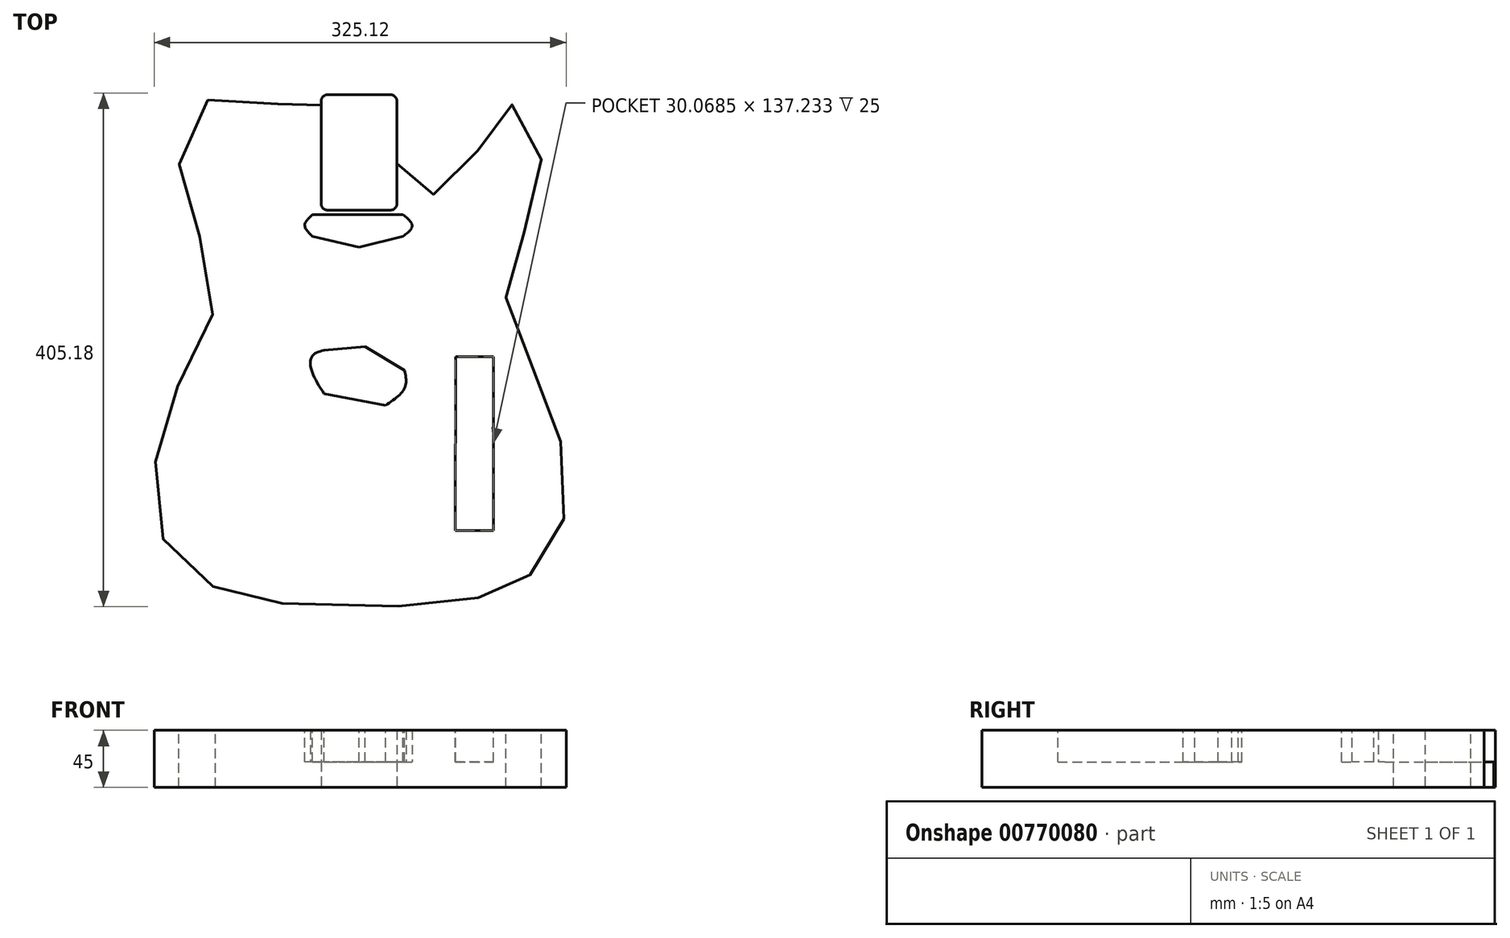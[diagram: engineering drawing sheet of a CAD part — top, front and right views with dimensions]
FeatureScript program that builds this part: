
annotation { "Feature Type Name" : "Feature", "Feature Type Description" : "" }
export const myFeature = defineFeature(function(context is Context, id is Id, definition is map)
    precondition{}
    {
        {
            var Q0;
            Q0=qCreatedBy(makeId("Top.planeOp"),FACE);
            var sketch = newSketch(context, id + "F0", { "sketchPlane" : qUnion([Q0])});
            skLineSegment(sketch, "E0.bottom", {"start": v(170, 207.5) * mm, "end": v(-170, 207.5) * mm});
            skLineSegment(sketch, "E0.top", {"start": v(170, -207.5) * mm, "end": v(-170, -207.5) * mm});
            skLineSegment(sketch, "E0.left", {"start": v(170, 207.5) * mm, "end": v(170, -207.5) * mm});
            skLineSegment(sketch, "E0.right", {"start": v(-170, 207.5) * mm, "end": v(-170, -207.5) * mm});
            skPoint(sketch, "E0.middle", {"position": v(0, 0) * mm});
            skLineSegment(sketch, "E1", {"start": v(-29.87, 193.13) * mm, "end": v(-29.87, 115.48) * mm});
            skLineSegment(sketch, "E2", {"start": v(-24.87, 110.48) * mm, "end": v(24.87, 110.48) * mm});
            skLineSegment(sketch, "E3", {"start": v(29.87, 115.48) * mm, "end": v(29.87, 147.1) * mm});
            skFitSpline(sketch, "E4", {"points": [v(29.87, 147.1) * mm, v(32.83, 137.03) * mm, v(40.54, 127.4) * mm, v(48.46, 123.11) * mm, v(60.88, 123.11) * mm, v(72.66, 126.75) * mm, v(84.65, 138.96) * mm, v(94.07, 158.01) * mm, v(99.85, 174.71) * mm, v(106.7, 187.78) * mm, v(117.41, 193.56) * mm, v(126.83, 191.42) * mm, v(137.54, 179.21) * mm, v(143.1, 164.44) * mm, v(143.1, 135.96) * mm, v(139.68, 119.26) * mm, v(132.4, 97.63) * mm, v(124.26, 79) * mm, v(119.13, 64.01) * mm, v(116.13, 46.45) * mm, v(118.27, 27.6) * mm, v(127.05, 6.2) * mm, v(137.75, -15.43) * mm, v(147.4, -36.63) * mm, v(154.88, -58.25) * mm, v(161.52, -82.88) * mm, v(163.45, -106.43) * mm, v(162.6, -128.49) * mm, v(156.81, -149.26) * mm, v(148.46, -163.18) * mm, v(137.54, -175.17) * mm, v(129.4, -181.6) * mm, v(117.63, -188.02) * mm, v(105.85, -192.3) * mm, v(92.15, -195.72) * mm, v(74.59, -198.94) * mm, v(55.53, -200.86) * mm, v(0, -202.36) * mm, v(-51.53, -200.22) * mm, v(-76.37, -198.5) * mm, v(-95, -194.87) * mm, v(-112.56, -187.8) * mm, v(-127.55, -179.66) * mm, v(-143.82, -166.17) * mm, v(-153.89, -150.11) * mm, v(-160.1, -134.7) * mm, v(-161.38, -101.08) * mm, v(-160.1, -84.38) * mm, v(-154.53, -60.4) * mm, v(-146.18, -35.99) * mm, v(-136.97, -15.86) * mm, v(-123.9, 8.55) * mm, v(-115.13, 29.97) * mm, v(-114.27, 59.3) * mm, v(-121.12, 79.43) * mm, v(-130.76, 101.06) * mm, v(-138.04, 124.82) * mm, v(-141.25, 141.74) * mm, v(-141.25, 166.15) * mm, v(-133.76, 184.56) * mm, v(-118.77, 197.63) * mm, v(-99.5, 202.76) * mm, v(-77.87, 199.55) * mm, v(-60.95, 192.7) * mm, v(-45.75, 185) * mm, v(-40.83, 183.5) * mm, v(-34.19, 186.7) * mm, v(-29.87, 193.13) * mm], "startDerivative": vector(179, -913.5) * mm, "endDerivative": vector(365.97, 729.24) * mm});
            skLineSegment(sketch, "E5", {"start": v(-29.87, 193.13) * mm, "end": v(-29.87, 196.51) * mm});
            skLineSegment(sketch, "E6", {"start": v(29.87, 147.1) * mm, "end": v(29.87, 196.51) * mm});
            skLineSegment(sketch, "E7", {"start": v(-24.87, 201.51) * mm, "end": v(24.87, 201.51) * mm});
            skPoint(sketch, "E8.visualSharp", {"position": v(-29.87, 201.51) * mm});
            skArc(sketch, "E8.filletArc", {"start": v(-24.87, 201.51) * mm, "mid": v(-28.4, 200.05) * mm, "end": v(-29.87, 196.51) * mm});
            skPoint(sketch, "E9.visualSharp", {"position": v(29.87, 201.51) * mm});
            skArc(sketch, "E9.filletArc", {"start": v(29.87, 196.51) * mm, "mid": v(28.4, 200.05) * mm, "end": v(24.87, 201.51) * mm});
            skPoint(sketch, "E10.visualSharp", {"position": v(-29.87, 110.48) * mm});
            skArc(sketch, "E10.filletArc", {"start": v(-29.87, 115.48) * mm, "mid": v(-28.4, 111.94) * mm, "end": v(-24.87, 110.48) * mm});
            skPoint(sketch, "E11.visualSharp", {"position": v(29.87, 110.48) * mm});
            skArc(sketch, "E11.filletArc", {"start": v(24.87, 110.48) * mm, "mid": v(28.4, 111.94) * mm, "end": v(29.87, 115.48) * mm});
            skLineSegment(sketch, "E12", {"start": v(0, 0) * mm, "end": v(0, 0) * mm});
            skLineSegment(sketch, "E13", {"start": v(49.42, 0) * mm, "end": v(50, 0) * mm, "construction": true});
            skPoint(sketch, "E14.trimOffspring.end.orphan", {"position": v(0, 201.51) * mm});
            skPoint(sketch, "E15.start.orphan", {"position": v(0, -202.26) * mm});
            skLineSegment(sketch, "E16", {"start": v(163.22, -99.32) * mm, "end": v(181.56, -99.32) * mm, "construction": true});
            skLineSegment(sketch, "E17", {"start": v(-161.35, -100.15) * mm, "end": v(-180.86, -100.15) * mm, "construction": true});
            skPoint(sketch, "E18.orphan", {"position": v(48.46, -201.22) * mm});
            skPoint(sketch, "E19.orphan", {"position": v(-50, -200.3) * mm});
            skPoint(sketch, "E20.orphan", {"position": v(-50, -100.15) * mm});
            skPoint(sketch, "E21.start.orphan", {"position": v(-50, 0) * mm});
            skSolve(sketch);
        }
        {
            var Q0;
            Q0=makeQuery(id+"F0.imprint","IMPRINT",FACE,{"disambiguationData":[TD([[makeQuery(id+"F0.imprint","IMPRINT",EDGE,{"derivedFrom":sQuery(id+"F0.wireOp",EDGE,"E1")}),1.0]])]});
            extrude(context, id + "F1", {"entities" : qUnion([Q0]), "depth" : 20 * mm, "offsetDistance" : 25 * mm});
        }
        {
            var Q0;
            Q0=makeQuery(id+"F0.imprint","IMPRINT",FACE,{"disambiguationData":[TD([[makeQuery(id+"F0.imprint","IMPRINT",EDGE,{"derivedFrom":sQuery(id+"F0.wireOp",EDGE,"E1")}),-1.0]])]});
            extrude(context, id + "F2", {"entities" : qUnion([Q0]), "operationType" : NewBodyOperationType.ADD, "depth" : 45 * mm, "offsetDistance" : 25 * mm});
        }
        {
            var Q0;
            Q0=makeQuery(id+"F2.opExtrude","CAP_FACE",FACE,{"disambiguationData":[OSD([sQuery(id+"F0.wireOp",EDGE,"E1"),sQuery(id+"F0.wireOp",EDGE,"E2"),sQuery(id+"F0.wireOp",EDGE,"E3"),sQuery(id+"F0.wireOp",EDGE,"E4"),sQuery(id+"F0.wireOp",EDGE,"E10.filletArc"),sQuery(id+"F0.wireOp",EDGE,"E11.filletArc")])],"isStart":false});
            var sketch = newSketch(context, id + "F3", { "sketchPlane" : qUnion([Q0])});
            skLineSegment(sketch, "E22", {"start": v(-36.68, 106.89) * mm, "end": v(34.75, 106.89) * mm});
            skFitSpline(sketch, "E23", {"points": [v(34.75, 106.89) * mm, v(42, 98.18) * mm, v(34.75, 89.76) * mm], "startDerivative": vector(21.74, -17.44) * mm, "endDerivative": vector(-21.81, -16.82) * mm});
            skLineSegment(sketch, "E24", {"start": v(34.75, 89.76) * mm, "end": v(0, 81.34) * mm});
            skLineSegment(sketch, "E25", {"start": v(0, 81.34) * mm, "end": v(-36.68, 89.76) * mm});
            skFitSpline(sketch, "E26", {"points": [v(-36.68, 106.89) * mm, v(-42.78, 98.47) * mm, v(-36.68, 89.76) * mm], "startDerivative": vector(-18.33, -16.84) * mm, "endDerivative": vector(18.26, -17.42) * mm});
            skLineSegment(sketch, "E27", {"start": v(76.35, -5.23) * mm, "end": v(106.18, -5.23) * mm});
            skLineSegment(sketch, "E28", {"start": v(106.18, -5.23) * mm, "end": v(106.18, -141.47) * mm});
            skLineSegment(sketch, "E29", {"start": v(106.18, -141.47) * mm, "end": v(106.18, -142.46) * mm});
            skLineSegment(sketch, "E30", {"start": v(106.18, -142.46) * mm, "end": v(76.12, -142.46) * mm});
            skLineSegment(sketch, "E31", {"start": v(76.12, -142.46) * mm, "end": v(76.35, -5.23) * mm});
            skLineSegment(sketch, "E32", {"start": v(4.9, 2.69) * mm, "end": v(36.07, -16.1) * mm});
            skFitSpline(sketch, "E33", {"points": [v(36.07, -16.1) * mm, v(36.07, -29.8) * mm, v(20.9, -43.64) * mm], "startDerivative": vector(6.19, -31.64) * mm, "endDerivative": vector(-35.13, -23.7) * mm});
            skLineSegment(sketch, "E34", {"start": v(20.9, -43.64) * mm, "end": v(-27.57, -34.4) * mm});
            skFitSpline(sketch, "E35", {"points": [v(-27.57, -34.4) * mm, v(-37.95, -13.8) * mm, v(-36.3, -4.07) * mm, v(-27.57, 0) * mm], "startDerivative": vector(-31.31, 50.02) * mm, "endDerivative": vector(36.18, 10.02) * mm});
            skLineSegment(sketch, "E36", {"start": v(-27.57, 0) * mm, "end": v(4.9, 2.69) * mm});
            skSolve(sketch);
        }
        {
            var Q0;
            Q0=makeQuery(id+"F3.imprint","IMPRINT",FACE,{"disambiguationData":[TD([[makeQuery(id+"F3.imprint","IMPRINT",EDGE,{"derivedFrom":sQuery(id+"F3.wireOp",EDGE,"E32")}),-1.0]])]});
            var Q1;
            Q1=makeQuery(id+"F3.imprint","IMPRINT",FACE,{"disambiguationData":[TD([[makeQuery(id+"F3.imprint","IMPRINT",EDGE,{"derivedFrom":sQuery(id+"F3.wireOp",EDGE,"E22")}),-1.0]])]});
            var Q2;
            Q2=makeQuery(id+"F3.imprint","IMPRINT",FACE,{"disambiguationData":[TD([[makeQuery(id+"F3.imprint","IMPRINT",EDGE,{"derivedFrom":sQuery(id+"F3.wireOp",EDGE,"E27")}),-1.0]])]});
            extrude(context, id + "F4", {"entities" : qUnion([Q0, Q1, Q2]), "operationType" : NewBodyOperationType.REMOVE, "oppositeDirection" : true, "depth" : 25 * mm, "offsetDistance" : 25 * mm});
        }
    });
